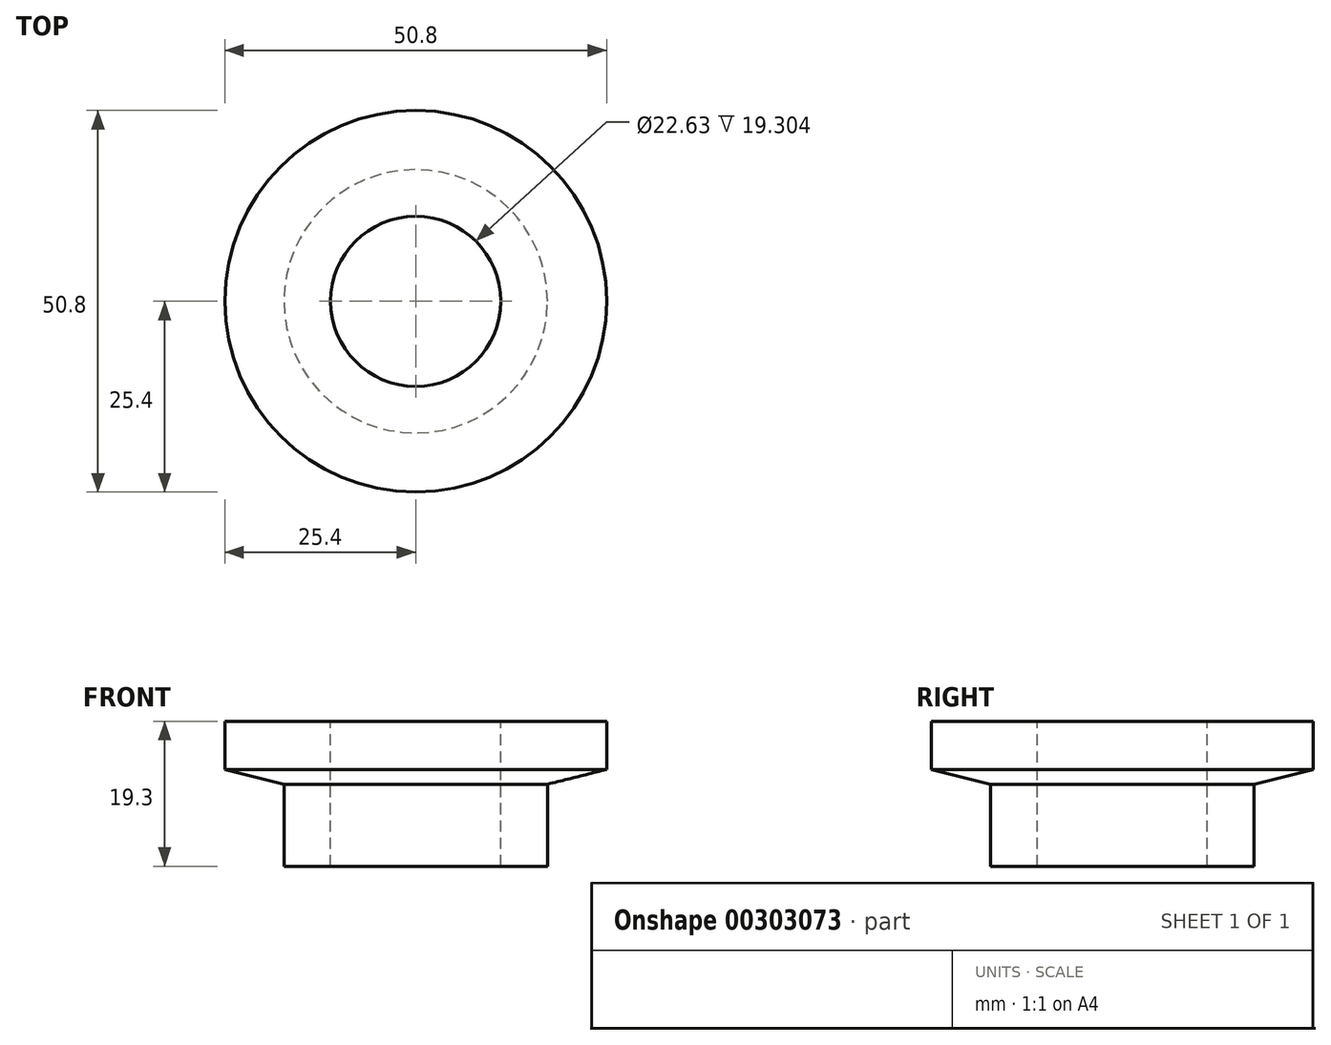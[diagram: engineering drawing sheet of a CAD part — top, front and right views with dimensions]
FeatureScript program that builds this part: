
annotation { "Feature Type Name" : "Feature", "Feature Type Description" : "" }
export const myFeature = defineFeature(function(context is Context, id is Id, definition is map)
    precondition{}
    {
        {
            var Q0;
            Q0=qCreatedBy(makeId("Front.planeOp"),FACE);
            var sketch = newSketch(context, id + "F0", { "sketchPlane" : qUnion([Q0])});
            skLineSegment(sketch, "E0", {"start": v(0, 15.77) * mm, "end": v(0, -16.78) * mm, "construction": true});
            skLineSegment(sketch, "E1", {"start": v(0, 9.65) * mm, "end": v(-25.4, 9.65) * mm});
            skLineSegment(sketch, "E2", {"start": v(-25.4, 9.65) * mm, "end": v(-25.4, 3.23) * mm});
            skLineSegment(sketch, "E3", {"start": v(-25.4, 3.23) * mm, "end": v(-17.53, 1.27) * mm});
            skLineSegment(sketch, "E4", {"start": v(-17.53, 1.27) * mm, "end": v(-17.53, -9.65) * mm});
            skLineSegment(sketch, "E5", {"start": v(-17.53, -9.65) * mm, "end": v(0, -9.65) * mm});
            skLineSegment(sketch, "E6", {"start": v(-11.32, 9.65) * mm, "end": v(-11.32, -9.65) * mm});
            skLineSegment(sketch, "E7.MirrorCS", {"start": v(25.4, 9.65) * mm, "end": v(25.4, 3.23) * mm});
            skLineSegment(sketch, "E8.MirrorCS", {"start": v(11.32, 9.65) * mm, "end": v(11.32, -9.65) * mm});
            skLineSegment(sketch, "E9.MirrorCS", {"start": v(17.53, -9.65) * mm, "end": v(0, -9.65) * mm});
            skLineSegment(sketch, "E10.MirrorCS", {"start": v(17.53, 1.27) * mm, "end": v(17.53, -9.65) * mm});
            skLineSegment(sketch, "E11.MirrorCS", {"start": v(0, 9.65) * mm, "end": v(25.4, 9.65) * mm});
            skLineSegment(sketch, "E12.MirrorCS", {"start": v(25.4, 3.23) * mm, "end": v(17.53, 1.27) * mm});
            skSolve(sketch);
        }
        {
            var Q0;
            {var subQ1=sQuery(id+"F0.wireOp",EDGE,"E2");Q0=makeQuery(id+"F0.imprint","IMPRINT",FACE,{"disambiguationData":[TD([[makeQuery(id+"F0.imprint","IMPRINT",EDGE,{"derivedFrom":subQ1}),1.0]])]});}
            var Q1;
            Q1=sQuery(id+"F0.wireOp",EDGE,"E0");
            revolve(context, id + "F1", {"entities" : qUnion([Q0]), "axis" : qUnion([Q1]), "revolveType" : RevolveType.FULL});
        }
    });
